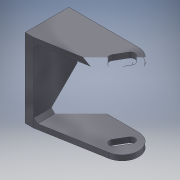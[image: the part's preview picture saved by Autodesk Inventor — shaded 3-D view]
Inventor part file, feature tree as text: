
AUTODESK INVENTOR PART (.ipt)
format: ipt  version: 2016 (Build 200138000, 138)  size: 153,088 bytes
history: native  units: mm
features: extrude x2, sketch x2, mirror x1, chamfer x1
ambient origin geometry x8: Origin, YZ Plane, XZ Plane, XY Plane, X Axis, Y Axis, Z Axis, Center Point
bodies: Body1 (feature_tree)
feature tree (6):
  extrude  "Extrusion2"  Depth=4.8mm
  extrude  "Extrusion3"  Depth=3.0mm
  mirror  "Mirror1"
  chamfer  "Chamfer1"  Distance=14.835299mm
  sketch  "Sketch2"  dims[d11=25.0mm d12=4.8mm]
  sketch  "Sketch3"  dims[d13=45.0mm d14=0.0mm d15=40.0mm d16=14.835299mm d17=5.0mm d18=7.0mm d19=30.0deg d20=3.0mm d21=0.0mm d22=2.0mm d23=2.0mm d24=45.0deg]
